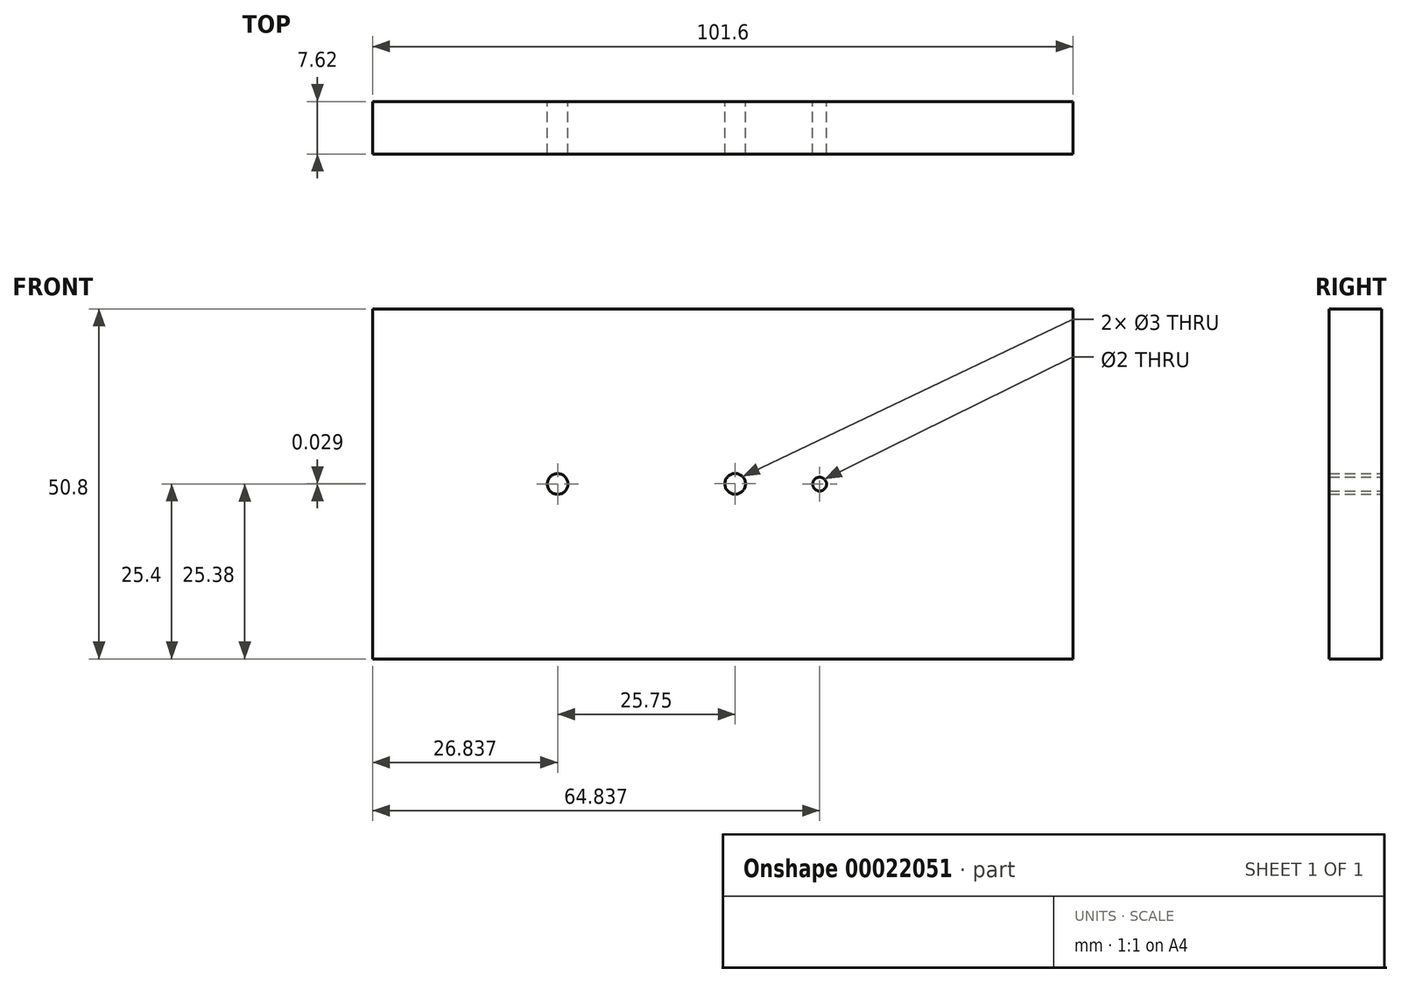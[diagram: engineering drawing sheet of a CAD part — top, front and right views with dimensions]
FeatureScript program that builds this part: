
annotation { "Feature Type Name" : "Feature", "Feature Type Description" : "" }
export const myFeature = defineFeature(function(context is Context, id is Id, definition is map)
    precondition{}
    {
        {
            var Q0;
            Q0=qCreatedBy(makeId("Front.planeOp"),FACE);
            var sketch = newSketch(context, id + "F0", { "sketchPlane" : qUnion([Q0])});
            skLineSegment(sketch, "E0.bottom", {"start": v(-149.37, -14.87) * mm, "end": v(-47.77, -14.87) * mm});
            skLineSegment(sketch, "E0.top", {"start": v(-149.37, -65.67) * mm, "end": v(-47.77, -65.67) * mm});
            skLineSegment(sketch, "E0.left", {"start": v(-149.37, -14.87) * mm, "end": v(-149.37, -65.67) * mm});
            skLineSegment(sketch, "E0.right", {"start": v(-47.77, -14.87) * mm, "end": v(-47.77, -65.67) * mm});
            skCircle(sketch, "E1", {"center": v(-122.53, -40.27) * mm, "radius": 1.5 * mm});
            skCircle(sketch, "E2", {"center": v(-96.78, -40.24) * mm, "radius": 1.5 * mm});
            skCircle(sketch, "E3", {"center": v(-84.53, -40.29) * mm, "radius": 1 * mm});
            skSolve(sketch);
        }
        {
            var Q0;
            Q0=makeQuery(id+"F0.imprint","IMPRINT",FACE,{"disambiguationData":[TD([[makeQuery(id+"F0.imprint","IMPRINT",EDGE,{"derivedFrom":sQuery(id+"F0.wireOp",EDGE,"E0.bottom")}),-1.0]])]});
            extrude(context, id + "F1", {"entities" : qUnion([Q0]), "depth" : 7.62 * mm});
        }
    });
